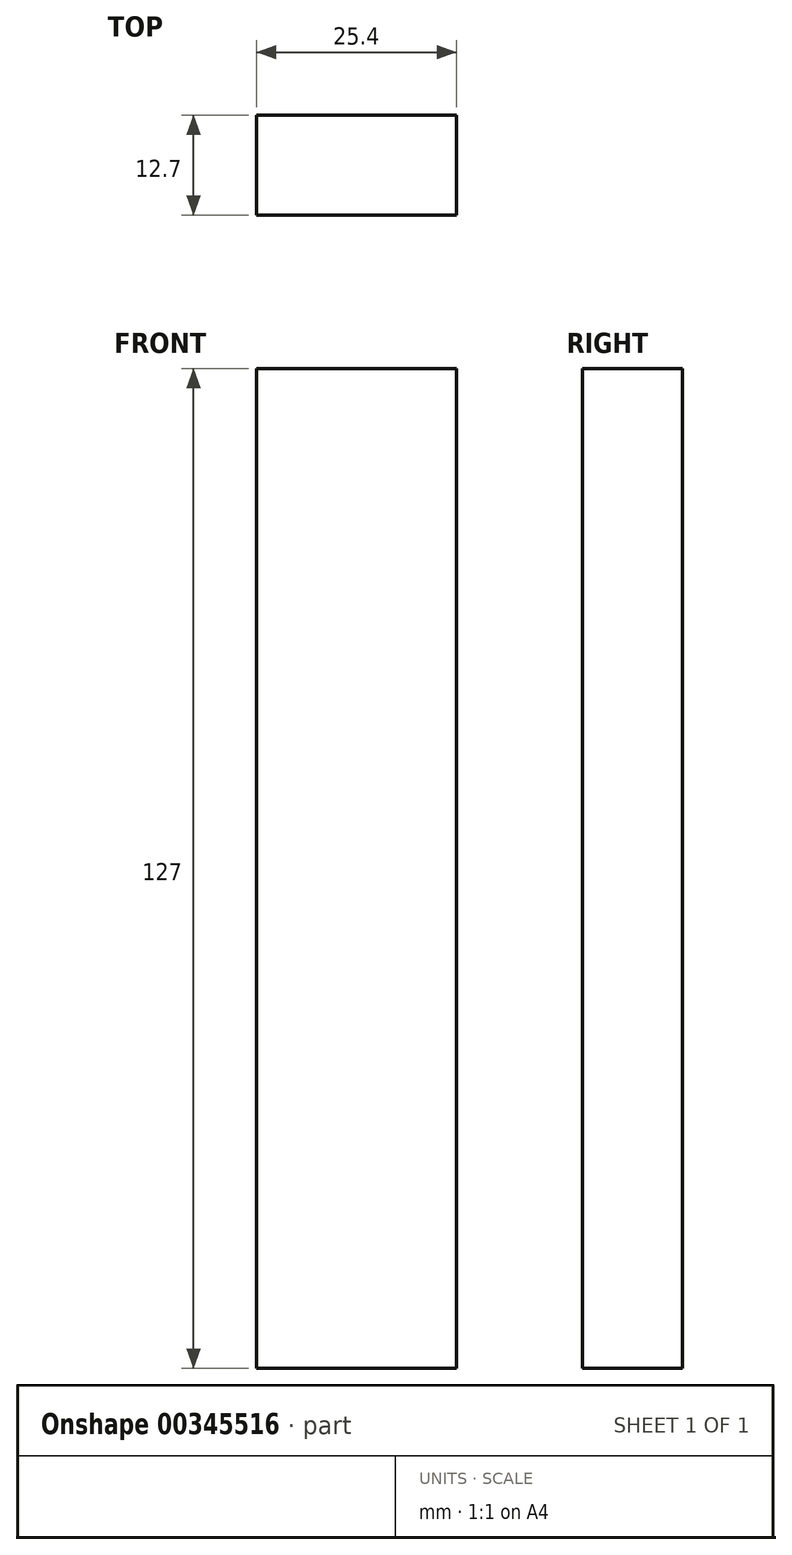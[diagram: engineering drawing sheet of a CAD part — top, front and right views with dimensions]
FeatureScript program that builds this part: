
annotation { "Feature Type Name" : "Feature", "Feature Type Description" : "" }
export const myFeature = defineFeature(function(context is Context, id is Id, definition is map)
    precondition{}
    {
        {
            var Q0;
            Q0=qCreatedBy(makeId("Top.planeOp"),FACE);
            var sketch = newSketch(context, id + "F0", { "sketchPlane" : qUnion([Q0])});
            skLineSegment(sketch, "E0.bottom", {"start": v(12.7, 6.35) * mm, "end": v(-12.7, 6.35) * mm});
            skLineSegment(sketch, "E0.top", {"start": v(12.7, -6.35) * mm, "end": v(-12.7, -6.35) * mm});
            skLineSegment(sketch, "E0.left", {"start": v(12.7, 6.35) * mm, "end": v(12.7, -6.35) * mm});
            skLineSegment(sketch, "E0.right", {"start": v(-12.7, 6.35) * mm, "end": v(-12.7, -6.35) * mm});
            skPoint(sketch, "E0.middle", {"position": v(0, 0) * mm});
            skSolve(sketch);
        }
        {
            var Q0;
            Q0=makeQuery(id+"F0.imprint","IMPRINT",FACE,{"disambiguationData":[TD([[makeQuery(id+"F0.imprint","IMPRINT",EDGE,{"derivedFrom":sQuery(id+"F0.wireOp",EDGE,"E0.bottom")}),1.0]])]});
            extrude(context, id + "F1", {"entities" : qUnion([Q0]), "depth" : 127 * mm});
        }
    });
